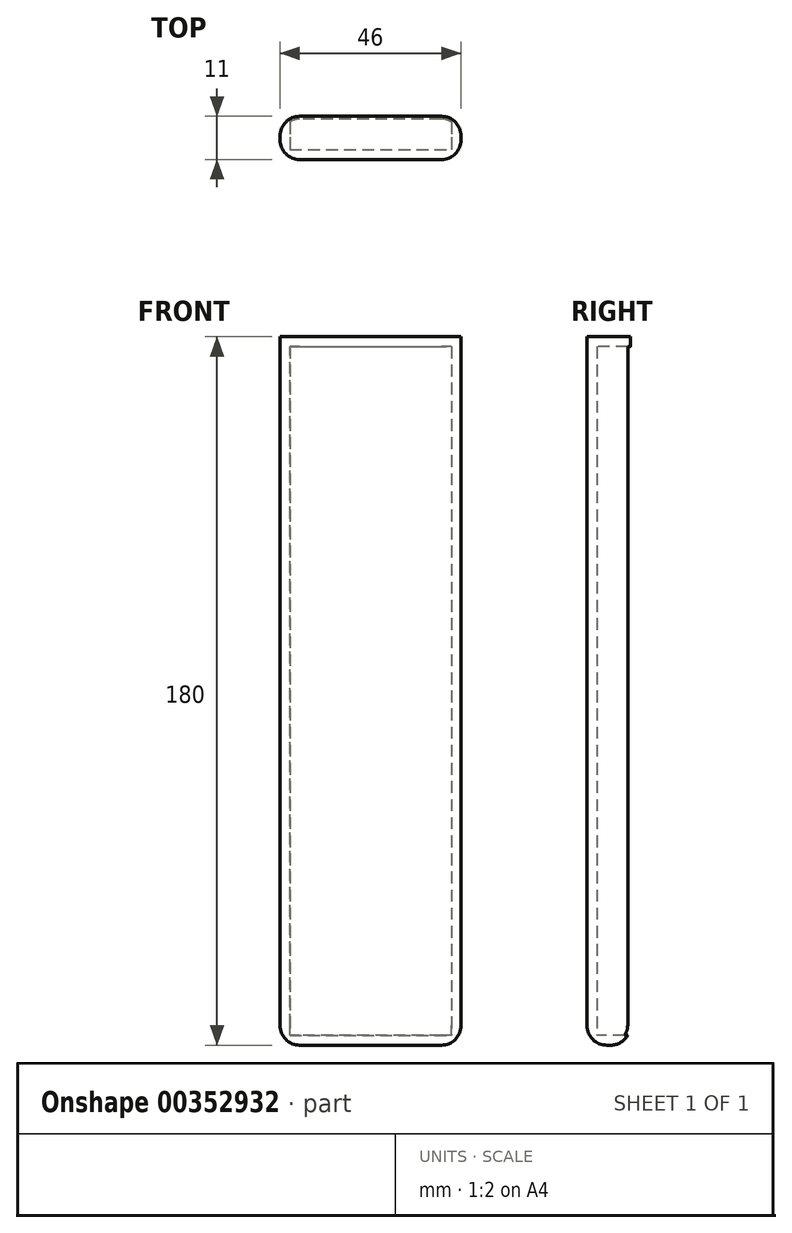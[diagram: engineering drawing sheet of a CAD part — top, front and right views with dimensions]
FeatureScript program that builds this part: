
annotation { "Feature Type Name" : "Feature", "Feature Type Description" : "" }
export const myFeature = defineFeature(function(context is Context, id is Id, definition is map)
    precondition{}
    {
        {
            var Q0;
            Q0=qCreatedBy(makeId("Top.planeOp"),FACE);
            var sketch = newSketch(context, id + "F0", { "sketchPlane" : qUnion([Q0])});
            skLineSegment(sketch, "E0.bottom", {"start": v(0, 0) * mm, "end": v(46, 0) * mm});
            skLineSegment(sketch, "E0.top", {"start": v(0, -11) * mm, "end": v(46, -11) * mm});
            skLineSegment(sketch, "E0.left", {"start": v(0, 0) * mm, "end": v(0, -11) * mm});
            skLineSegment(sketch, "E0.right", {"start": v(46, 0) * mm, "end": v(46, -11) * mm});
            skSolve(sketch);
        }
        {
            var Q0;
            Q0 = qSketchRegion(id + "F0", true);
            extrude(context, id + "F1", {"entities" : qUnion([Q0]), "depth" : 180 * mm, "offsetDistance" : 25 * mm});
        }
        {
            var Q0;
            Q0=makeQuery(id+"F1.opExtrude","SWEPT_FACE",FACE,{"disambiguationData":[OSD([sQuery(id+"F0.wireOp",EDGE,"E0.bottom")])]});
            shell(context, id + "F2", {"entities" : qUnion([Q0]), "thickness" : 2.5 * mm});
        }
        {
            var Q0;
            Q0=makeQuery(id+"F1.opExtrude","CAP_EDGE",EDGE,{"disambiguationData":[OSD([sQuery(id+"F0.wireOp",EDGE,"E0.bottom")])],"isStart":true});
            fillet(context, id + "F3", {"entities" : qUnion([Q0]), "tangentPropagation" : true, "radius" : 5 * mm, "defaultsChanged" : false, "vertexSettings" : [], "allowEdgeOverflow" : false});
        }
        {
            var Q0;
            Q0=makeQuery(id+"F1.opExtrude","CAP_EDGE",EDGE,{"disambiguationData":[OSD([sQuery(id+"F0.wireOp",EDGE,"E0.top")])],"isStart":true});
            fillet(context, id + "F4", {"entities" : qUnion([Q0]), "tangentPropagation" : true, "radius" : 5 * mm, "defaultsChanged" : false, "vertexSettings" : [], "allowEdgeOverflow" : false});
        }
        {
            var Q0;
            Q0=makeQuery(id+"F1.opExtrude","SWEPT_EDGE",EDGE,{"disambiguationData":[OSD([sQuery(id+"F0.wireOp",EDGE,"E0.top"),sQuery(id+"F0.wireOp",EDGE,"E0.left")])]});
            var Q1;
            Q1=makeQuery(id+"F1.opExtrude","SWEPT_EDGE",EDGE,{"disambiguationData":[OSD([sQuery(id+"F0.wireOp",EDGE,"E0.top"),sQuery(id+"F0.wireOp",EDGE,"E0.right")])]});
            fillet(context, id + "F5", {"entities" : qUnion([Q0, Q1]), "tangentPropagation" : true, "radius" : 5 * mm, "defaultsChanged" : false, "vertexSettings" : [], "allowEdgeOverflow" : false});
        }
    });
